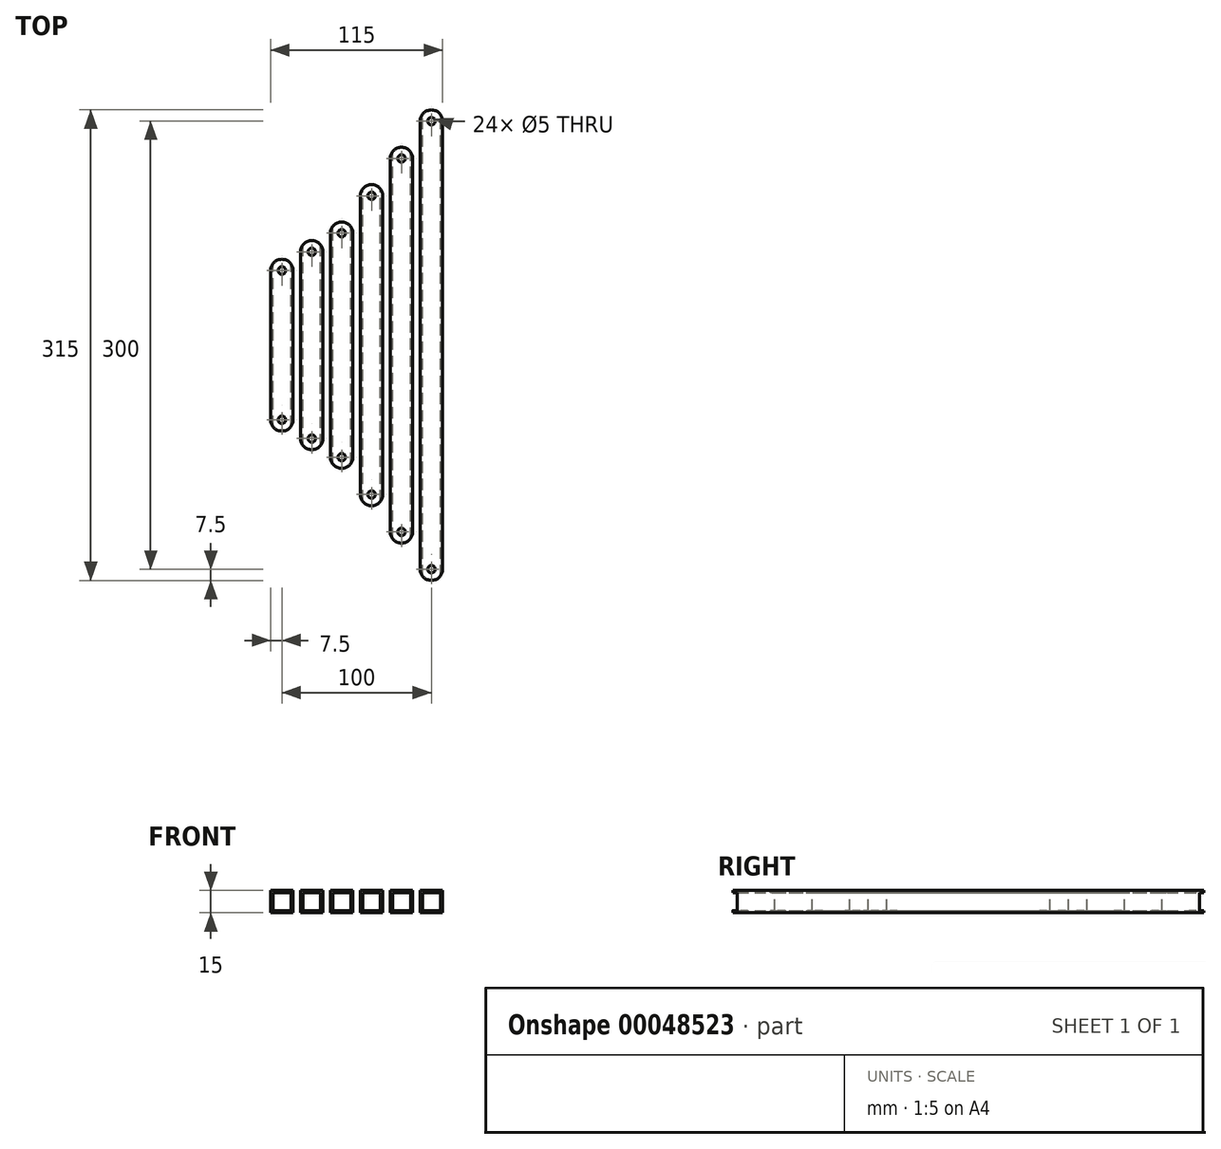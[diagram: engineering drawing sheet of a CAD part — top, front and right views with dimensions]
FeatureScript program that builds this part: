
annotation { "Feature Type Name" : "Feature", "Feature Type Description" : "" }
export const myFeature = defineFeature(function(context is Context, id is Id, definition is map)
    precondition{}
    {
        {
            var Q0;
            Q0=qCreatedBy(makeId("Front.planeOp"),FACE);
            var sketch = newSketch(context, id + "F0", { "sketchPlane" : qUnion([Q0])});
            skPoint(sketch, "E0", {"position": v(-50, 0) * mm});
            skLineSegment(sketch, "E1.bottom", {"start": v(-56, 6) * mm, "end": v(-44, 6) * mm});
            skLineSegment(sketch, "E1.top", {"start": v(-56, -6) * mm, "end": v(-44, -6) * mm});
            skLineSegment(sketch, "E1.left", {"start": v(-56, 6) * mm, "end": v(-56, -6) * mm});
            skLineSegment(sketch, "E1.right", {"start": v(-44, 6) * mm, "end": v(-44, -6) * mm});
            skLineSegment(sketch, "E2.bottom", {"start": v(-57.5, 7.5) * mm, "end": v(-42.5, 7.5) * mm});
            skLineSegment(sketch, "E2.top", {"start": v(-57.5, -7.5) * mm, "end": v(-42.5, -7.5) * mm});
            skLineSegment(sketch, "E2.left", {"start": v(-57.5, 7.5) * mm, "end": v(-57.5, -7.5) * mm});
            skLineSegment(sketch, "E2.right", {"start": v(-42.5, 7.5) * mm, "end": v(-42.5, -7.5) * mm});
            skLineSegment(sketch, "E3", {"start": v(-50, 0) * mm, "end": v(-30, 0) * mm, "construction": true});
            skLineSegment(sketch, "E4", {"start": v(-30, 0) * mm, "end": v(-10, 0) * mm, "construction": true});
            skLineSegment(sketch, "E5", {"start": v(-10, 0) * mm, "end": v(10, 0) * mm, "construction": true});
            skLineSegment(sketch, "E6", {"start": v(10, 0) * mm, "end": v(30, 0) * mm, "construction": true});
            skLineSegment(sketch, "E7", {"start": v(30, 0) * mm, "end": v(50, 0) * mm, "construction": true});
            skLineSegment(sketch, "E8.bottom", {"start": v(-36, 6) * mm, "end": v(-24, 6) * mm});
            skLineSegment(sketch, "E8.top", {"start": v(-36, -6) * mm, "end": v(-24, -6) * mm});
            skLineSegment(sketch, "E9.bottom", {"start": v(-37.5, 7.5) * mm, "end": v(-22.5, 7.5) * mm});
            skLineSegment(sketch, "E8.right", {"start": v(-24, 6) * mm, "end": v(-24, -6) * mm});
            skLineSegment(sketch, "E8.left", {"start": v(-36, 6) * mm, "end": v(-36, -6) * mm});
            skPoint(sketch, "E10", {"position": v(-30, 0) * mm});
            skLineSegment(sketch, "E9.left", {"start": v(-37.5, 7.5) * mm, "end": v(-37.5, -7.5) * mm});
            skLineSegment(sketch, "E9.top", {"start": v(-37.5, -7.5) * mm, "end": v(-22.5, -7.5) * mm});
            skLineSegment(sketch, "E9.right", {"start": v(-22.5, 7.5) * mm, "end": v(-22.5, -7.5) * mm});
            skLineSegment(sketch, "E11.bottom", {"start": v(-16, 6) * mm, "end": v(-4, 6) * mm});
            skLineSegment(sketch, "E11.top", {"start": v(-16, -6) * mm, "end": v(-4, -6) * mm});
            skLineSegment(sketch, "E12.bottom", {"start": v(-17.5, 7.5) * mm, "end": v(-2.5, 7.5) * mm});
            skLineSegment(sketch, "E11.right", {"start": v(-4, 6) * mm, "end": v(-4, -6) * mm});
            skLineSegment(sketch, "E11.left", {"start": v(-16, 6) * mm, "end": v(-16, -6) * mm});
            skPoint(sketch, "E13", {"position": v(-10, 0) * mm});
            skLineSegment(sketch, "E12.left", {"start": v(-17.5, 7.5) * mm, "end": v(-17.5, -7.5) * mm});
            skLineSegment(sketch, "E12.top", {"start": v(-17.5, -7.5) * mm, "end": v(-2.5, -7.5) * mm});
            skLineSegment(sketch, "E12.right", {"start": v(-2.5, 7.5) * mm, "end": v(-2.5, -7.5) * mm});
            skLineSegment(sketch, "E14.bottom", {"start": v(4, 6) * mm, "end": v(16, 6) * mm});
            skLineSegment(sketch, "E14.top", {"start": v(4, -6) * mm, "end": v(16, -6) * mm});
            skLineSegment(sketch, "E15.bottom", {"start": v(2.5, 7.5) * mm, "end": v(17.5, 7.5) * mm});
            skLineSegment(sketch, "E14.right", {"start": v(16, 6) * mm, "end": v(16, -6) * mm});
            skLineSegment(sketch, "E14.left", {"start": v(4, 6) * mm, "end": v(4, -6) * mm});
            skPoint(sketch, "E16", {"position": v(10, 0) * mm});
            skLineSegment(sketch, "E15.left", {"start": v(2.5, 7.5) * mm, "end": v(2.5, -7.5) * mm});
            skLineSegment(sketch, "E15.top", {"start": v(2.5, -7.5) * mm, "end": v(17.5, -7.5) * mm});
            skLineSegment(sketch, "E15.right", {"start": v(17.5, 7.5) * mm, "end": v(17.5, -7.5) * mm});
            skLineSegment(sketch, "E17.bottom", {"start": v(24, 6) * mm, "end": v(36, 6) * mm});
            skLineSegment(sketch, "E17.top", {"start": v(24, -6) * mm, "end": v(36, -6) * mm});
            skLineSegment(sketch, "E18.bottom", {"start": v(22.5, 7.5) * mm, "end": v(37.5, 7.5) * mm});
            skLineSegment(sketch, "E17.right", {"start": v(36, 6) * mm, "end": v(36, -6) * mm});
            skLineSegment(sketch, "E17.left", {"start": v(24, 6) * mm, "end": v(24, -6) * mm});
            skPoint(sketch, "E19", {"position": v(30, 0) * mm});
            skLineSegment(sketch, "E18.left", {"start": v(22.5, 7.5) * mm, "end": v(22.5, -7.5) * mm});
            skLineSegment(sketch, "E18.top", {"start": v(22.5, -7.5) * mm, "end": v(37.5, -7.5) * mm});
            skLineSegment(sketch, "E18.right", {"start": v(37.5, 7.5) * mm, "end": v(37.5, -7.5) * mm});
            skLineSegment(sketch, "E20.bottom", {"start": v(44, 6) * mm, "end": v(56, 6) * mm});
            skLineSegment(sketch, "E20.top", {"start": v(44, -6) * mm, "end": v(56, -6) * mm});
            skLineSegment(sketch, "E21.bottom", {"start": v(42.5, 7.5) * mm, "end": v(57.5, 7.5) * mm});
            skLineSegment(sketch, "E20.right", {"start": v(56, 6) * mm, "end": v(56, -6) * mm});
            skLineSegment(sketch, "E20.left", {"start": v(44, 6) * mm, "end": v(44, -6) * mm});
            skPoint(sketch, "E22", {"position": v(50, 0) * mm});
            skLineSegment(sketch, "E21.left", {"start": v(42.5, 7.5) * mm, "end": v(42.5, -7.5) * mm});
            skLineSegment(sketch, "E21.top", {"start": v(42.5, -7.5) * mm, "end": v(57.5, -7.5) * mm});
            skLineSegment(sketch, "E21.right", {"start": v(57.5, 7.5) * mm, "end": v(57.5, -7.5) * mm});
            skSolve(sketch);
        }
        {
            var Q0;
            Q0=makeQuery(id+"F0.imprint","IMPRINT",FACE,{"disambiguationData":[TD([[makeQuery(id+"F0.imprint","IMPRINT",EDGE,{"derivedFrom":sQuery(id+"F0.wireOp",EDGE,"E1.bottom")}),1.0]])]});
            extrude(context, id + "F1", {"entities" : qUnion([Q0]), "endBound" : BoundingType.SYMMETRIC, "depth" : 115 * mm});
        }
        {
            var Q0;
            Q0=makeQuery(id+"F0.imprint","IMPRINT",FACE,{"disambiguationData":[TD([[makeQuery(id+"F0.imprint","IMPRINT",EDGE,{"derivedFrom":sQuery(id+"F0.wireOp",EDGE,"E8.bottom")}),1.0]])]});
            extrude(context, id + "F2", {"entities" : qUnion([Q0]), "endBound" : BoundingType.SYMMETRIC, "depth" : 140 * mm});
        }
        {
            var Q0;
            Q0=makeQuery(id+"F0.imprint","IMPRINT",FACE,{"disambiguationData":[TD([[makeQuery(id+"F0.imprint","IMPRINT",EDGE,{"derivedFrom":sQuery(id+"F0.wireOp",EDGE,"E11.bottom")}),1.0]])]});
            extrude(context, id + "F3", {"entities" : qUnion([Q0]), "endBound" : BoundingType.SYMMETRIC, "depth" : 165 * mm});
        }
        {
            var Q0;
            Q0=makeQuery(id+"F0.imprint","IMPRINT",FACE,{"disambiguationData":[TD([[makeQuery(id+"F0.imprint","IMPRINT",EDGE,{"derivedFrom":sQuery(id+"F0.wireOp",EDGE,"E14.bottom")}),1.0]])]});
            extrude(context, id + "F4", {"entities" : qUnion([Q0]), "endBound" : BoundingType.SYMMETRIC, "depth" : 215 * mm});
        }
        {
            var Q0;
            Q0=makeQuery(id+"F0.imprint","IMPRINT",FACE,{"disambiguationData":[TD([[makeQuery(id+"F0.imprint","IMPRINT",EDGE,{"derivedFrom":sQuery(id+"F0.wireOp",EDGE,"E17.bottom")}),1.0]])]});
            extrude(context, id + "F5", {"entities" : qUnion([Q0]), "endBound" : BoundingType.SYMMETRIC, "depth" : 265 * mm});
        }
        {
            var Q0;
            Q0=makeQuery(id+"F0.imprint","IMPRINT",FACE,{"disambiguationData":[TD([[makeQuery(id+"F0.imprint","IMPRINT",EDGE,{"derivedFrom":sQuery(id+"F0.wireOp",EDGE,"E20.bottom")}),1.0]])]});
            extrude(context, id + "F6", {"entities" : qUnion([Q0]), "endBound" : BoundingType.SYMMETRIC, "depth" : 315 * mm});
        }
        {
            var Q0;
            Q0=makeQuery(id+"F1.opExtrude","SWEPT_FACE",FACE,{"disambiguationData":[OSD([sQuery(id+"F0.wireOp",EDGE,"E2.bottom")])]});
            var sketch = newSketch(context, id + "F7", { "sketchPlane" : qUnion([Q0])});
            skLineSegment(sketch, "E23.0.0", {"start": v(-42.5, 57.5) * mm, "end": v(-57.5, 57.5) * mm});
            skLineSegment(sketch, "E23.0.1", {"start": v(-57.5, 57.5) * mm, "end": v(-57.5, -57.5) * mm});
            skLineSegment(sketch, "E23.0.2", {"start": v(-57.5, -57.5) * mm, "end": v(-42.5, -57.5) * mm});
            skLineSegment(sketch, "E23.0.3", {"start": v(-42.5, -57.5) * mm, "end": v(-42.5, 57.5) * mm});
            skLineSegment(sketch, "E24.0.0", {"start": v(-22.5, 70) * mm, "end": v(-37.5, 70) * mm});
            skLineSegment(sketch, "E24.0.1", {"start": v(-37.5, 70) * mm, "end": v(-37.5, -70) * mm});
            skLineSegment(sketch, "E24.0.2", {"start": v(-37.5, -70) * mm, "end": v(-22.5, -70) * mm});
            skLineSegment(sketch, "E24.0.3", {"start": v(-22.5, -70) * mm, "end": v(-22.5, 70) * mm});
            skLineSegment(sketch, "E25.0.0", {"start": v(-2.5, 82.5) * mm, "end": v(-17.5, 82.5) * mm});
            skLineSegment(sketch, "E25.0.1", {"start": v(-17.5, 82.5) * mm, "end": v(-17.5, -82.5) * mm});
            skLineSegment(sketch, "E25.0.2", {"start": v(-17.5, -82.5) * mm, "end": v(-2.5, -82.5) * mm});
            skLineSegment(sketch, "E25.0.3", {"start": v(-2.5, -82.5) * mm, "end": v(-2.5, 82.5) * mm});
            skLineSegment(sketch, "E26.0.0", {"start": v(17.5, 107.5) * mm, "end": v(2.5, 107.5) * mm});
            skLineSegment(sketch, "E26.0.1", {"start": v(2.5, 107.5) * mm, "end": v(2.5, -107.5) * mm});
            skLineSegment(sketch, "E26.0.2", {"start": v(2.5, -107.5) * mm, "end": v(17.5, -107.5) * mm});
            skLineSegment(sketch, "E26.0.3", {"start": v(17.5, -107.5) * mm, "end": v(17.5, 107.5) * mm});
            skLineSegment(sketch, "E27.0.0", {"start": v(37.5, 132.5) * mm, "end": v(22.5, 132.5) * mm});
            skLineSegment(sketch, "E27.0.1", {"start": v(22.5, 132.5) * mm, "end": v(22.5, -132.5) * mm});
            skLineSegment(sketch, "E27.0.2", {"start": v(22.5, -132.5) * mm, "end": v(37.5, -132.5) * mm});
            skLineSegment(sketch, "E27.0.3", {"start": v(37.5, -132.5) * mm, "end": v(37.5, 132.5) * mm});
            skLineSegment(sketch, "E28.0.0", {"start": v(57.5, 157.5) * mm, "end": v(42.5, 157.5) * mm});
            skLineSegment(sketch, "E28.0.1", {"start": v(42.5, 157.5) * mm, "end": v(42.5, -157.5) * mm});
            skLineSegment(sketch, "E28.0.2", {"start": v(42.5, -157.5) * mm, "end": v(57.5, -157.5) * mm});
            skLineSegment(sketch, "E28.0.3", {"start": v(57.5, -157.5) * mm, "end": v(57.5, 157.5) * mm});
            skCircle(sketch, "E29", {"center": v(-10, 75) * mm, "radius": 7.5 * mm});
            skCircle(sketch, "E30", {"center": v(10, -100) * mm, "radius": 7.5 * mm});
            skCircle(sketch, "E31", {"center": v(-30, 62.5) * mm, "radius": 7.5 * mm});
            skCircle(sketch, "E32", {"center": v(-30, -62.5) * mm, "radius": 7.5 * mm});
            skCircle(sketch, "E33", {"center": v(10, 100) * mm, "radius": 7.5 * mm});
            skCircle(sketch, "E34", {"center": v(30, 125) * mm, "radius": 7.5 * mm});
            skCircle(sketch, "E35", {"center": v(30, -125) * mm, "radius": 7.5 * mm});
            skCircle(sketch, "E36", {"center": v(-10, -75) * mm, "radius": 7.5 * mm});
            skCircle(sketch, "E37", {"center": v(-50, 50) * mm, "radius": 7.5 * mm});
            skCircle(sketch, "E38", {"center": v(-50, -50) * mm, "radius": 7.5 * mm});
            skCircle(sketch, "E39", {"center": v(50, 150) * mm, "radius": 7.5 * mm});
            skCircle(sketch, "E40", {"center": v(50, -150) * mm, "radius": 7.5 * mm});
            skCircle(sketch, "E41", {"center": v(-50, 50) * mm, "radius": 2.5 * mm});
            skCircle(sketch, "E42", {"center": v(-30, 62.5) * mm, "radius": 2.5 * mm});
            skCircle(sketch, "E43", {"center": v(-10, 75) * mm, "radius": 2.5 * mm});
            skCircle(sketch, "E44", {"center": v(10, 100) * mm, "radius": 2.5 * mm});
            skCircle(sketch, "E45", {"center": v(30, 125) * mm, "radius": 2.5 * mm});
            skCircle(sketch, "E46", {"center": v(50, 150) * mm, "radius": 2.5 * mm});
            skCircle(sketch, "E47", {"center": v(-50, -50) * mm, "radius": 2.5 * mm});
            skCircle(sketch, "E48", {"center": v(-30, -62.5) * mm, "radius": 2.5 * mm});
            skCircle(sketch, "E49", {"center": v(-10, -75) * mm, "radius": 2.5 * mm});
            skCircle(sketch, "E50", {"center": v(10, -100) * mm, "radius": 2.5 * mm});
            skCircle(sketch, "E51", {"center": v(30, -125) * mm, "radius": 2.5 * mm});
            skCircle(sketch, "E52", {"center": v(50, -150) * mm, "radius": 2.5 * mm});
            skSolve(sketch);
        }
        {
            var Q0;
            {var subQ1=sQuery(id+"F7.wireOp",EDGE,"E28.0.3");var subQ3=sQuery(id+"F7.wireOp",EDGE,"E28.0.2");var subQ5=makeQuery(id+"F7.imprint","INTERSECT",VERTEX,{"derivedFrom":[subQ3,subQ1]});Q0=makeQuery(id+"F7.imprint","IMPRINT",FACE,{"disambiguationData":[TD([[makeQuery(id+"F7.imprint","IMPRINT",EDGE,{"disambiguationData":[TD([[subQ5,1.0]])],"derivedFrom":subQ3}),1.0]])]});}
            var Q1;
            {var subQ1=sQuery(id+"F7.wireOp",EDGE,"E28.0.2");var subQ3=sQuery(id+"F7.wireOp",EDGE,"E28.0.1");var subQ5=makeQuery(id+"F7.imprint","INTERSECT",VERTEX,{"derivedFrom":[subQ3,subQ1]});Q1=makeQuery(id+"F7.imprint","IMPRINT",FACE,{"disambiguationData":[TD([[makeQuery(id+"F7.imprint","IMPRINT",EDGE,{"disambiguationData":[TD([[subQ5,1.0]])],"derivedFrom":subQ3}),1.0]])]});}
            var Q2;
            Q2=makeQuery(id+"F7.imprint","IMPRINT",FACE,{"disambiguationData":[TD([[makeQuery(id+"F7.imprint","IMPRINT",EDGE,{"derivedFrom":sQuery(id+"F7.wireOp",EDGE,"E51")}),1.0]])]});
            var Q3;
            {var subQ0=sQuery(id+"F7.wireOp",EDGE,"E27.0.3");var subQ3=sQuery(id+"F7.wireOp",EDGE,"E27.0.2");var subQ4=makeQuery(id+"F7.imprint","INTERSECT",VERTEX,{"derivedFrom":[subQ3,subQ0]});Q3=makeQuery(id+"F7.imprint","IMPRINT",FACE,{"disambiguationData":[TD([[makeQuery(id+"F7.imprint","IMPRINT",EDGE,{"disambiguationData":[TD([[subQ4,1.0]])],"derivedFrom":subQ3}),1.0]])]});}
            var Q4;
            Q4=makeQuery(id+"F7.imprint","IMPRINT",FACE,{"disambiguationData":[TD([[makeQuery(id+"F7.imprint","IMPRINT",EDGE,{"derivedFrom":sQuery(id+"F7.wireOp",EDGE,"E50")}),1.0]])]});
            var Q5;
            {var subQ1=sQuery(id+"F7.wireOp",EDGE,"E26.0.3");var subQ3=sQuery(id+"F7.wireOp",EDGE,"E26.0.2");var subQ5=makeQuery(id+"F7.imprint","INTERSECT",VERTEX,{"derivedFrom":[subQ3,subQ1]});Q5=makeQuery(id+"F7.imprint","IMPRINT",FACE,{"disambiguationData":[TD([[makeQuery(id+"F7.imprint","IMPRINT",EDGE,{"disambiguationData":[TD([[subQ5,1.0]])],"derivedFrom":subQ3}),1.0]])]});}
            var Q6;
            {var subQ0=sQuery(id+"F7.wireOp",EDGE,"E26.0.2");var subQ3=sQuery(id+"F7.wireOp",EDGE,"E26.0.1");var subQ4=makeQuery(id+"F7.imprint","INTERSECT",VERTEX,{"derivedFrom":[subQ3,subQ0]});Q6=makeQuery(id+"F7.imprint","IMPRINT",FACE,{"disambiguationData":[TD([[makeQuery(id+"F7.imprint","IMPRINT",EDGE,{"disambiguationData":[TD([[subQ4,1.0]])],"derivedFrom":subQ3}),1.0]])]});}
            var Q7;
            Q7=makeQuery(id+"F7.imprint","IMPRINT",FACE,{"disambiguationData":[TD([[makeQuery(id+"F7.imprint","IMPRINT",EDGE,{"derivedFrom":sQuery(id+"F7.wireOp",EDGE,"E48")}),1.0]])]});
            var Q8;
            Q8=makeQuery(id+"F7.imprint","IMPRINT",FACE,{"disambiguationData":[TD([[makeQuery(id+"F7.imprint","IMPRINT",EDGE,{"derivedFrom":sQuery(id+"F7.wireOp",EDGE,"E47")}),1.0]])]});
            var Q9;
            Q9=makeQuery(id+"F7.imprint","IMPRINT",FACE,{"disambiguationData":[TD([[makeQuery(id+"F7.imprint","IMPRINT",EDGE,{"derivedFrom":sQuery(id+"F7.wireOp",EDGE,"E49")}),1.0]])]});
            var Q10;
            {var subQ0=sQuery(id+"F7.wireOp",EDGE,"E25.0.2");var subQ3=sQuery(id+"F7.wireOp",EDGE,"E25.0.1");var subQ4=makeQuery(id+"F7.imprint","INTERSECT",VERTEX,{"derivedFrom":[subQ3,subQ0]});Q10=makeQuery(id+"F7.imprint","IMPRINT",FACE,{"disambiguationData":[TD([[makeQuery(id+"F7.imprint","IMPRINT",EDGE,{"disambiguationData":[TD([[subQ4,1.0]])],"derivedFrom":subQ3}),1.0]])]});}
            var Q11;
            {var subQ1=sQuery(id+"F7.wireOp",EDGE,"E25.0.3");var subQ3=sQuery(id+"F7.wireOp",EDGE,"E25.0.2");var subQ5=makeQuery(id+"F7.imprint","INTERSECT",VERTEX,{"derivedFrom":[subQ3,subQ1]});Q11=makeQuery(id+"F7.imprint","IMPRINT",FACE,{"disambiguationData":[TD([[makeQuery(id+"F7.imprint","IMPRINT",EDGE,{"disambiguationData":[TD([[subQ5,1.0]])],"derivedFrom":subQ3}),1.0]])]});}
            var Q12;
            {var subQ1=sQuery(id+"F7.wireOp",EDGE,"E24.0.3");var subQ3=sQuery(id+"F7.wireOp",EDGE,"E24.0.2");var subQ5=makeQuery(id+"F7.imprint","INTERSECT",VERTEX,{"derivedFrom":[subQ3,subQ1]});Q12=makeQuery(id+"F7.imprint","IMPRINT",FACE,{"disambiguationData":[TD([[makeQuery(id+"F7.imprint","IMPRINT",EDGE,{"disambiguationData":[TD([[subQ5,1.0]])],"derivedFrom":subQ3}),1.0]])]});}
            var Q13;
            {var subQ0=sQuery(id+"F7.wireOp",EDGE,"E24.0.2");var subQ3=sQuery(id+"F7.wireOp",EDGE,"E24.0.1");var subQ4=makeQuery(id+"F7.imprint","INTERSECT",VERTEX,{"derivedFrom":[subQ3,subQ0]});Q13=makeQuery(id+"F7.imprint","IMPRINT",FACE,{"disambiguationData":[TD([[makeQuery(id+"F7.imprint","IMPRINT",EDGE,{"disambiguationData":[TD([[subQ4,1.0]])],"derivedFrom":subQ3}),1.0]])]});}
            var Q14;
            {var subQ1=sQuery(id+"F7.wireOp",EDGE,"E23.0.3");var subQ3=sQuery(id+"F7.wireOp",EDGE,"E23.0.2");var subQ5=makeQuery(id+"F7.imprint","INTERSECT",VERTEX,{"derivedFrom":[subQ3,subQ1]});Q14=makeQuery(id+"F7.imprint","IMPRINT",FACE,{"disambiguationData":[TD([[makeQuery(id+"F7.imprint","IMPRINT",EDGE,{"disambiguationData":[TD([[subQ5,1.0]])],"derivedFrom":subQ3}),1.0]])]});}
            var Q15;
            {var subQ0=sQuery(id+"F7.wireOp",EDGE,"E23.0.2");var subQ3=sQuery(id+"F7.wireOp",EDGE,"E23.0.1");var subQ4=makeQuery(id+"F7.imprint","INTERSECT",VERTEX,{"derivedFrom":[subQ3,subQ0]});Q15=makeQuery(id+"F7.imprint","IMPRINT",FACE,{"disambiguationData":[TD([[makeQuery(id+"F7.imprint","IMPRINT",EDGE,{"disambiguationData":[TD([[subQ4,-1.0]])],"derivedFrom":subQ3}),-1.0]])]});}
            var Q16;
            {var subQ1=sQuery(id+"F7.wireOp",EDGE,"E23.0.1");var subQ3=sQuery(id+"F7.wireOp",EDGE,"E23.0.0");var subQ5=makeQuery(id+"F7.imprint","INTERSECT",VERTEX,{"derivedFrom":[subQ3,subQ1]});Q16=makeQuery(id+"F7.imprint","IMPRINT",FACE,{"disambiguationData":[TD([[makeQuery(id+"F7.imprint","IMPRINT",EDGE,{"disambiguationData":[TD([[subQ5,-1.0]])],"derivedFrom":subQ3}),-1.0]])]});}
            var Q17;
            Q17=makeQuery(id+"F7.imprint","IMPRINT",FACE,{"disambiguationData":[TD([[makeQuery(id+"F7.imprint","IMPRINT",EDGE,{"derivedFrom":sQuery(id+"F7.wireOp",EDGE,"E41")}),1.0]])]});
            var Q18;
            {var subQ1=sQuery(id+"F7.wireOp",EDGE,"E23.0.3");var subQ3=sQuery(id+"F7.wireOp",EDGE,"E23.0.0");var subQ5=makeQuery(id+"F7.imprint","INTERSECT",VERTEX,{"derivedFrom":[subQ3,subQ1]});Q18=makeQuery(id+"F7.imprint","IMPRINT",FACE,{"disambiguationData":[TD([[makeQuery(id+"F7.imprint","IMPRINT",EDGE,{"disambiguationData":[TD([[subQ5,1.0]])],"derivedFrom":subQ3}),-1.0]])]});}
            var Q19;
            {var subQ0=sQuery(id+"F7.wireOp",EDGE,"E24.0.1");var subQ3=sQuery(id+"F7.wireOp",EDGE,"E24.0.0");var subQ4=makeQuery(id+"F7.imprint","INTERSECT",VERTEX,{"derivedFrom":[subQ3,subQ0]});Q19=makeQuery(id+"F7.imprint","IMPRINT",FACE,{"disambiguationData":[TD([[makeQuery(id+"F7.imprint","IMPRINT",EDGE,{"disambiguationData":[TD([[subQ4,1.0]])],"derivedFrom":subQ3}),1.0]])]});}
            var Q20;
            Q20=makeQuery(id+"F7.imprint","IMPRINT",FACE,{"disambiguationData":[TD([[makeQuery(id+"F7.imprint","IMPRINT",EDGE,{"derivedFrom":sQuery(id+"F7.wireOp",EDGE,"E42")}),1.0]])]});
            var Q21;
            {var subQ0=sQuery(id+"F7.wireOp",EDGE,"E24.0.3");var subQ3=sQuery(id+"F7.wireOp",EDGE,"E24.0.0");var subQ4=makeQuery(id+"F7.imprint","INTERSECT",VERTEX,{"derivedFrom":[subQ3,subQ0]});Q21=makeQuery(id+"F7.imprint","IMPRINT",FACE,{"disambiguationData":[TD([[makeQuery(id+"F7.imprint","IMPRINT",EDGE,{"disambiguationData":[TD([[subQ4,-1.0]])],"derivedFrom":subQ3}),1.0]])]});}
            var Q22;
            {var subQ1=sQuery(id+"F7.wireOp",EDGE,"E25.0.1");var subQ3=sQuery(id+"F7.wireOp",EDGE,"E25.0.0");var subQ5=makeQuery(id+"F7.imprint","INTERSECT",VERTEX,{"derivedFrom":[subQ3,subQ1]});Q22=makeQuery(id+"F7.imprint","IMPRINT",FACE,{"disambiguationData":[TD([[makeQuery(id+"F7.imprint","IMPRINT",EDGE,{"disambiguationData":[TD([[subQ5,1.0]])],"derivedFrom":subQ3}),1.0]])]});}
            var Q23;
            {var subQ0=sQuery(id+"F7.wireOp",EDGE,"E25.0.3");var subQ3=sQuery(id+"F7.wireOp",EDGE,"E25.0.0");var subQ4=makeQuery(id+"F7.imprint","INTERSECT",VERTEX,{"derivedFrom":[subQ3,subQ0]});Q23=makeQuery(id+"F7.imprint","IMPRINT",FACE,{"disambiguationData":[TD([[makeQuery(id+"F7.imprint","IMPRINT",EDGE,{"disambiguationData":[TD([[subQ4,-1.0]])],"derivedFrom":subQ3}),1.0]])]});}
            var Q24;
            Q24=makeQuery(id+"F7.imprint","IMPRINT",FACE,{"disambiguationData":[TD([[makeQuery(id+"F7.imprint","IMPRINT",EDGE,{"derivedFrom":sQuery(id+"F7.wireOp",EDGE,"E43")}),1.0]])]});
            var Q25;
            {var subQ0=sQuery(id+"F7.wireOp",EDGE,"E26.0.1");var subQ3=sQuery(id+"F7.wireOp",EDGE,"E26.0.0");var subQ4=makeQuery(id+"F7.imprint","INTERSECT",VERTEX,{"derivedFrom":[subQ3,subQ0]});Q25=makeQuery(id+"F7.imprint","IMPRINT",FACE,{"disambiguationData":[TD([[makeQuery(id+"F7.imprint","IMPRINT",EDGE,{"disambiguationData":[TD([[subQ4,1.0]])],"derivedFrom":subQ3}),1.0]])]});}
            var Q26;
            Q26=makeQuery(id+"F7.imprint","IMPRINT",FACE,{"disambiguationData":[TD([[makeQuery(id+"F7.imprint","IMPRINT",EDGE,{"derivedFrom":sQuery(id+"F7.wireOp",EDGE,"E44")}),1.0]])]});
            var Q27;
            {var subQ0=sQuery(id+"F7.wireOp",EDGE,"E26.0.3");var subQ3=sQuery(id+"F7.wireOp",EDGE,"E26.0.0");var subQ4=makeQuery(id+"F7.imprint","INTERSECT",VERTEX,{"derivedFrom":[subQ3,subQ0]});Q27=makeQuery(id+"F7.imprint","IMPRINT",FACE,{"disambiguationData":[TD([[makeQuery(id+"F7.imprint","IMPRINT",EDGE,{"disambiguationData":[TD([[subQ4,-1.0]])],"derivedFrom":subQ3}),1.0]])]});}
            var Q28;
            {var subQ1=sQuery(id+"F7.wireOp",EDGE,"E27.0.1");var subQ3=sQuery(id+"F7.wireOp",EDGE,"E27.0.0");var subQ5=makeQuery(id+"F7.imprint","INTERSECT",VERTEX,{"derivedFrom":[subQ3,subQ1]});Q28=makeQuery(id+"F7.imprint","IMPRINT",FACE,{"disambiguationData":[TD([[makeQuery(id+"F7.imprint","IMPRINT",EDGE,{"disambiguationData":[TD([[subQ5,1.0]])],"derivedFrom":subQ3}),1.0]])]});}
            var Q29;
            Q29=makeQuery(id+"F7.imprint","IMPRINT",FACE,{"disambiguationData":[TD([[makeQuery(id+"F7.imprint","IMPRINT",EDGE,{"derivedFrom":sQuery(id+"F7.wireOp",EDGE,"E45")}),1.0]])]});
            var Q30;
            {var subQ1=sQuery(id+"F7.wireOp",EDGE,"E27.0.3");var subQ3=sQuery(id+"F7.wireOp",EDGE,"E27.0.0");var subQ5=makeQuery(id+"F7.imprint","INTERSECT",VERTEX,{"derivedFrom":[subQ3,subQ1]});Q30=makeQuery(id+"F7.imprint","IMPRINT",FACE,{"disambiguationData":[TD([[makeQuery(id+"F7.imprint","IMPRINT",EDGE,{"disambiguationData":[TD([[subQ5,-1.0]])],"derivedFrom":subQ3}),1.0]])]});}
            var Q31;
            {var subQ1=sQuery(id+"F7.wireOp",EDGE,"E28.0.1");var subQ3=sQuery(id+"F7.wireOp",EDGE,"E28.0.0");var subQ5=makeQuery(id+"F7.imprint","INTERSECT",VERTEX,{"derivedFrom":[subQ3,subQ1]});Q31=makeQuery(id+"F7.imprint","IMPRINT",FACE,{"disambiguationData":[TD([[makeQuery(id+"F7.imprint","IMPRINT",EDGE,{"disambiguationData":[TD([[subQ5,1.0]])],"derivedFrom":subQ3}),1.0]])]});}
            var Q32;
            {var subQ0=sQuery(id+"F7.wireOp",EDGE,"E28.0.3");var subQ3=sQuery(id+"F7.wireOp",EDGE,"E28.0.0");var subQ4=makeQuery(id+"F7.imprint","INTERSECT",VERTEX,{"derivedFrom":[subQ3,subQ0]});Q32=makeQuery(id+"F7.imprint","IMPRINT",FACE,{"disambiguationData":[TD([[makeQuery(id+"F7.imprint","IMPRINT",EDGE,{"disambiguationData":[TD([[subQ4,-1.0]])],"derivedFrom":subQ3}),1.0]])]});}
            var Q33;
            Q33=makeQuery(id+"F7.imprint","IMPRINT",FACE,{"disambiguationData":[TD([[makeQuery(id+"F7.imprint","IMPRINT",EDGE,{"derivedFrom":sQuery(id+"F7.wireOp",EDGE,"E52")}),1.0]])]});
            var Q34;
            Q34=makeQuery(id+"F7.imprint","IMPRINT",FACE,{"disambiguationData":[TD([[makeQuery(id+"F7.imprint","IMPRINT",EDGE,{"derivedFrom":sQuery(id+"F7.wireOp",EDGE,"E46")}),1.0]])]});
            var Q35;
            {var subQ1=sQuery(id+"F7.wireOp",EDGE,"E27.0.2");var subQ3=sQuery(id+"F7.wireOp",EDGE,"E27.0.1");var subQ5=makeQuery(id+"F7.imprint","INTERSECT",VERTEX,{"derivedFrom":[subQ3,subQ1]});Q35=makeQuery(id+"F7.imprint","IMPRINT",FACE,{"disambiguationData":[TD([[makeQuery(id+"F7.imprint","IMPRINT",EDGE,{"disambiguationData":[TD([[subQ5,1.0]])],"derivedFrom":subQ3}),1.0]])]});}
            var Q36;
            Q36=makeQuery(id+"F1.opExtrude","SWEPT_FACE",FACE,{"disambiguationData":[OSD([sQuery(id+"F0.wireOp",EDGE,"E2.top")])]});
            extrude(context, id + "F8", {"entities" : qUnion([Q0, Q1, Q2, Q3, Q4, Q5, Q6, Q7, Q8, Q9, Q10, Q11, Q12, Q13, Q14, Q15, Q16, Q17, Q18, Q19, Q20, Q21, Q22, Q23, Q24, Q25, Q26, Q27, Q28, Q29, Q30, Q31, Q32, Q33, Q34, Q35]), "operationType" : NewBodyOperationType.REMOVE, "endBound" : BoundingType.UP_TO_SURFACE, "oppositeDirection" : true, "endBoundEntityFace" : qUnion([Q36]), "depth" : 25 * mm});
        }
    });
